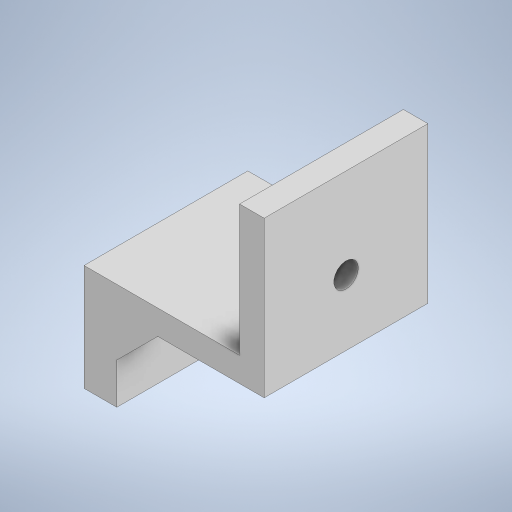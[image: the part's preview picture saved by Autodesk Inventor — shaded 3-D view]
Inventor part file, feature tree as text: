
AUTODESK INVENTOR PART (.ipt)
format: ipt  version: 2023 (Build 270158000, 158)  size: 272,384 bytes
history: native  units: in
note: dims shown in document units (in); Inventor stores cm internally (conversion verified against a paired STEP export)
features: extrude x7, sketch x7
ambient origin geometry x8: Origin, YZ Plane, XZ Plane, XY Plane, X Axis, Y Axis, Z Axis, Center Point
bodies: Solid1 (feature_tree)
feature tree (14):
  extrude  "Extrusion1"  Depth=0.748in
  extrude  "Extrusion4"  Depth=0.1181in
  extrude  "Extrusion5"  Depth=0.7874in TaperAngle=0.0deg
  extrude  "Extrusion6"  Depth=0.1575in
  extrude  "Extrusion7"  Depth=0.7874in TaperAngle=0.0deg
  extrude  "Extrusion8"  Depth=0.3937in
  extrude  "Extrusion9"  TaperAngle=0.0deg  [1 undecoded]
  sketch  "Sketch1"  dims[d0=0.8661in d1=0.748in]
  sketch  "Sketch4"  dims[d2=0.1181in d3=0.1181in]
  sketch  "Sketch5"  dims[d4=0.1181in d5=0.7874in d6=0.0in]
  sketch  "Sketch6"  dims[d15=0.0in d16=0.0in d17=0.1575in]
  sketch  "Sketch7"  dims[d18=0.3937in d19=0.7874in d20=0.0in]
  sketch  "Sketch8"  dims[d21=0.1969in d22=0.3937in]
  sketch  "Sketch9"  dims[d23=0.1969in d24=0.0in d25=0.0in d26=0.1969in d27=0.1969in d28=0.1575in d29=0.0in d30=0.1969in d31=0.1969in d32=0.1575in d33=0.0in d34=0.3937in d35=0.1969in d36=0.1181in d37=0.0in d38=0.0in]
note: 1 required parameter value undecoded (feature->parameter linkage not recoverable at this tier; creation-order binding heuristic only, values carry confidence <= 0.55)
